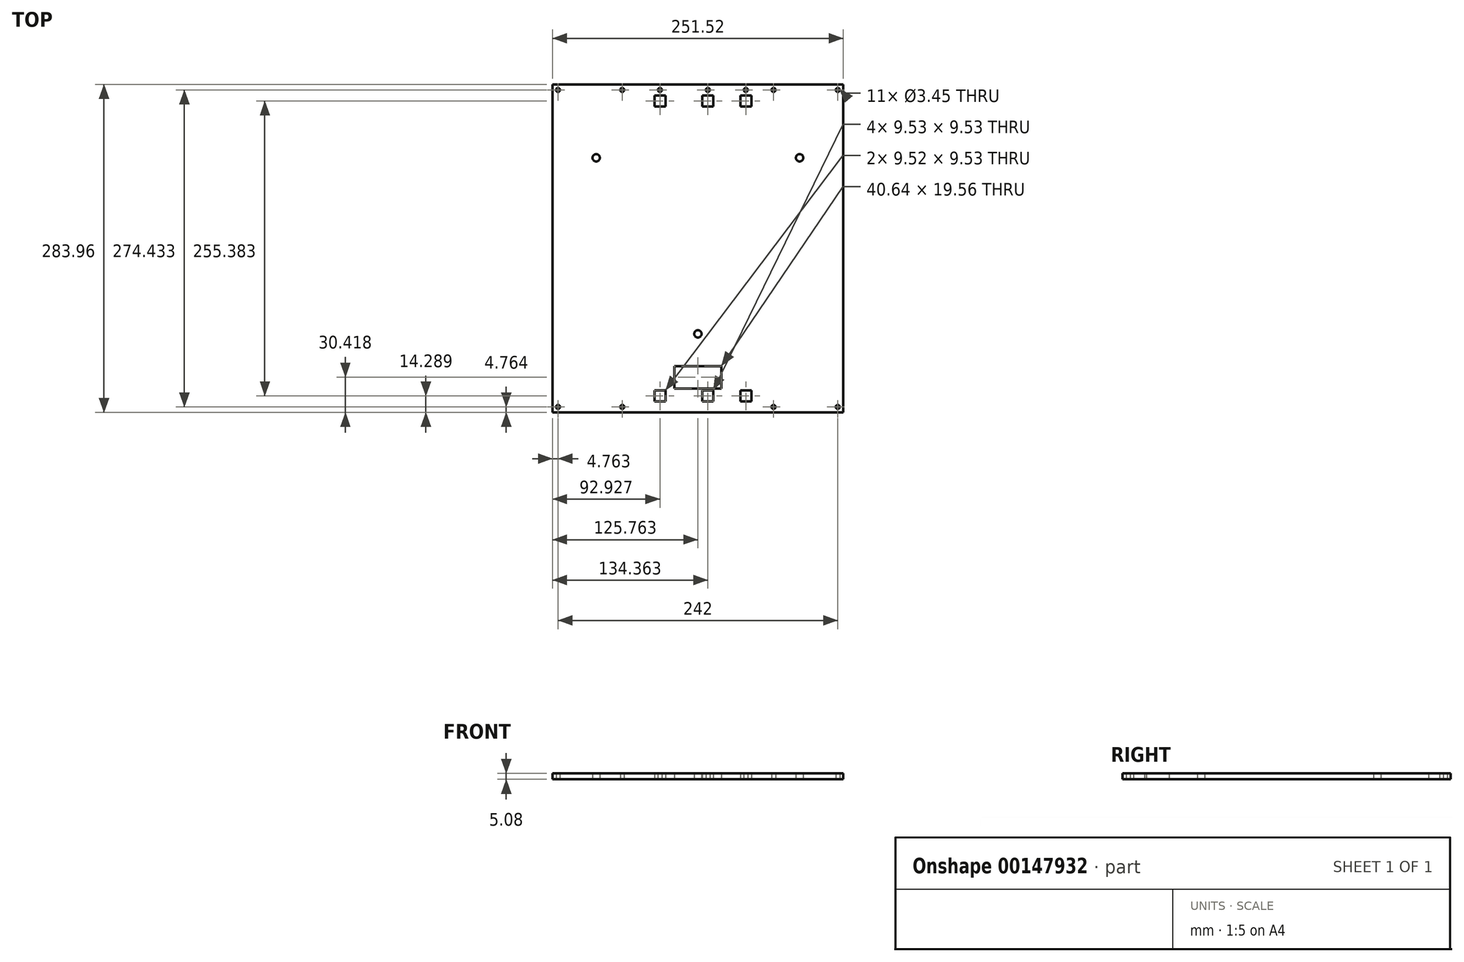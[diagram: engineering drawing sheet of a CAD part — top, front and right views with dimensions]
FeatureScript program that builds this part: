
annotation { "Feature Type Name" : "Feature", "Feature Type Description" : "" }
export const myFeature = defineFeature(function(context is Context, id is Id, definition is map)
    precondition{}
    {
        {
            var Q0;
            Q0=qCreatedBy(makeId("Top.planeOp"),FACE);
            var sketch = newSketch(context, id + "F0", { "sketchPlane" : qUnion([Q0])});
            skLineSegment(sketch, "E0.bottom", {"start": v(0, 0) * mm, "end": v(251.52, 0) * mm});
            skLineSegment(sketch, "E0.top", {"start": v(0, -283.96) * mm, "end": v(251.52, -283.96) * mm});
            skLineSegment(sketch, "E0.left", {"start": v(0, 0) * mm, "end": v(0, -283.96) * mm});
            skLineSegment(sketch, "E0.right", {"start": v(251.52, 0) * mm, "end": v(251.52, -283.96) * mm});
            skLineSegment(sketch, "E1", {"start": v(4.76, 0) * mm, "end": v(4.76, -4.76) * mm, "construction": true});
            skLineSegment(sketch, "E2", {"start": v(4.76, -4.76) * mm, "end": v(0, -4.76) * mm, "construction": true});
            skLineSegment(sketch, "E3", {"start": v(4.76, -4.76) * mm, "end": v(60.33, -4.76) * mm, "construction": true});
            skCircle(sketch, "E4", {"center": v(4.76, -4.76) * mm, "radius": 1.73 * mm});
            skCircle(sketch, "E5", {"center": v(60.33, -4.76) * mm, "radius": 1.73 * mm});
            skLineSegment(sketch, "E6", {"start": v(251.52, -4.76) * mm, "end": v(246.76, -4.76) * mm, "construction": true});
            skLineSegment(sketch, "E7", {"start": v(246.76, -4.76) * mm, "end": v(191.2, -4.76) * mm, "construction": true});
            skLineSegment(sketch, "E8", {"start": v(191.2, -4.76) * mm, "end": v(176.6, -4.76) * mm, "construction": true});
            skCircle(sketch, "E9", {"center": v(191.2, -4.76) * mm, "radius": 1.73 * mm});
            skCircle(sketch, "E10", {"center": v(246.76, -4.76) * mm, "radius": 1.73 * mm});
            skLineSegment(sketch, "E11", {"start": v(4.76, -283.96) * mm, "end": v(4.76, -279.2) * mm, "construction": true});
            skLineSegment(sketch, "E12", {"start": v(4.76, -279.2) * mm, "end": v(60.33, -279.2) * mm, "construction": true});
            skLineSegment(sketch, "E13", {"start": v(191.2, -279.2) * mm, "end": v(246.76, -279.2) * mm, "construction": true});
            skLineSegment(sketch, "E14", {"start": v(246.76, -279.2) * mm, "end": v(251.52, -279.2) * mm, "construction": true});
            skCircle(sketch, "E15", {"center": v(4.76, -279.2) * mm, "radius": 1.73 * mm});
            skCircle(sketch, "E16", {"center": v(60.33, -279.2) * mm, "radius": 1.73 * mm});
            skCircle(sketch, "E17", {"center": v(191.2, -279.2) * mm, "radius": 1.73 * mm});
            skCircle(sketch, "E18", {"center": v(246.76, -279.2) * mm, "radius": 1.73 * mm});
            skLineSegment(sketch, "E19", {"start": v(60.33, -4.76) * mm, "end": v(92.93, -4.76) * mm, "construction": true});
            skLineSegment(sketch, "E20", {"start": v(176.6, -4.76) * mm, "end": v(157.8, -4.76) * mm, "construction": true});
            skLineSegment(sketch, "E21", {"start": v(92.93, -4.76) * mm, "end": v(157.8, -4.76) * mm, "construction": true});
            skCircle(sketch, "E22", {"center": v(92.93, -4.76) * mm, "radius": 1.73 * mm});
            skCircle(sketch, "E23", {"center": v(134.36, -4.76) * mm, "radius": 1.73 * mm});
            skCircle(sketch, "E24", {"center": v(167.2, -4.76) * mm, "radius": 1.73 * mm});
            skLineSegment(sketch, "E25", {"start": v(92.93, -4.76) * mm, "end": v(92.93, -9.53) * mm, "construction": true});
            skLineSegment(sketch, "E26", {"start": v(134.36, -4.76) * mm, "end": v(134.36, -9.52) * mm, "construction": true});
            skLineSegment(sketch, "E27", {"start": v(167.2, -4.76) * mm, "end": v(167.2, -9.52) * mm, "construction": true});
            skLineSegment(sketch, "E28.bottom", {"start": v(88.17, -9.53) * mm, "end": v(97.7, -9.53) * mm});
            skLineSegment(sketch, "E28.top", {"start": v(88.17, -19.05) * mm, "end": v(97.7, -19.05) * mm});
            skLineSegment(sketch, "E28.left", {"start": v(88.17, -9.53) * mm, "end": v(88.17, -19.05) * mm});
            skLineSegment(sketch, "E28.right", {"start": v(97.7, -9.53) * mm, "end": v(97.7, -19.05) * mm});
            skLineSegment(sketch, "E29.bottom", {"start": v(129.6, -9.52) * mm, "end": v(139.12, -9.52) * mm});
            skLineSegment(sketch, "E29.top", {"start": v(129.6, -19.05) * mm, "end": v(139.12, -19.05) * mm});
            skLineSegment(sketch, "E29.left", {"start": v(129.6, -9.52) * mm, "end": v(129.6, -19.05) * mm});
            skLineSegment(sketch, "E29.right", {"start": v(139.12, -9.52) * mm, "end": v(139.12, -19.05) * mm});
            skLineSegment(sketch, "E30.bottom", {"start": v(162.43, -9.52) * mm, "end": v(171.96, -9.52) * mm});
            skLineSegment(sketch, "E30.top", {"start": v(162.43, -19.05) * mm, "end": v(171.96, -19.05) * mm});
            skLineSegment(sketch, "E30.left", {"start": v(162.43, -9.52) * mm, "end": v(162.43, -19.05) * mm});
            skLineSegment(sketch, "E30.right", {"start": v(171.96, -9.52) * mm, "end": v(171.96, -19.05) * mm});
            skLineSegment(sketch, "E31", {"start": v(125.76, 0) * mm, "end": v(125.76, -114.3) * mm, "construction": true});
            skCircle(sketch, "E32", {"center": v(125.76, -114.3) * mm, "radius": 114.3 * mm, "construction": true});
            skCircle(sketch, "E33.cCircle", {"center": v(125.76, -114.3) * mm, "radius": 50.8 * mm, "construction": true});
            skLineSegment(sketch, "E33.0", {"start": v(37.77, -63.5) * mm, "end": v(213.75, -63.5) * mm, "construction": true});
            skLineSegment(sketch, "E33.1", {"start": v(213.75, -63.5) * mm, "end": v(125.76, -215.9) * mm, "construction": true});
            skLineSegment(sketch, "E33.2", {"start": v(125.76, -215.9) * mm, "end": v(37.77, -63.5) * mm, "construction": true});
            skPoint(sketch, "E33.0.midPoint", {"position": v(125.76, -63.5) * mm});
            skCircle(sketch, "E34", {"center": v(213.75, -63.5) * mm, "radius": 12.7 * mm, "construction": true});
            skCircle(sketch, "E35", {"center": v(125.76, -215.9) * mm, "radius": 3.18 * mm});
            skCircle(sketch, "E36", {"center": v(37.77, -63.5) * mm, "radius": 3.18 * mm});
            skCircle(sketch, "E37", {"center": v(213.75, -63.5) * mm, "radius": 3.18 * mm});
            skLineSegment(sketch, "E38", {"start": v(125.76, -114.3) * mm, "end": v(125.76, -228.6) * mm, "construction": true});
            skLineSegment(sketch, "E39", {"start": v(125.76, -228.6) * mm, "end": v(125.76, -253.54) * mm, "construction": true});
            skLineSegment(sketch, "E40.bottom", {"start": v(146.08, -243.76) * mm, "end": v(105.44, -243.76) * mm});
            skLineSegment(sketch, "E40.top", {"start": v(146.08, -263.32) * mm, "end": v(105.44, -263.32) * mm});
            skLineSegment(sketch, "E40.left", {"start": v(146.08, -243.76) * mm, "end": v(146.08, -263.32) * mm});
            skLineSegment(sketch, "E40.right", {"start": v(105.44, -243.76) * mm, "end": v(105.44, -263.32) * mm});
            skPoint(sketch, "E40.middle", {"position": v(125.76, -253.54) * mm});
            skLineSegment(sketch, "E41", {"start": v(146.08, -253.54) * mm, "end": v(136.66, -253.54) * mm, "construction": true});
            skLineSegment(sketch, "E42", {"start": v(136.66, -253.54) * mm, "end": v(125.76, -114.3) * mm, "construction": true});
            skLineSegment(sketch, "E43", {"start": v(125.76, -263.32) * mm, "end": v(125.76, -283.96) * mm, "construction": true});
            skLineSegment(sketch, "E44", {"start": v(60.33, -279.2) * mm, "end": v(92.93, -279.2) * mm, "construction": true});
            skLineSegment(sketch, "E45", {"start": v(92.93, -279.2) * mm, "end": v(92.93, -274.43) * mm, "construction": true});
            skLineSegment(sketch, "E46", {"start": v(191.2, -279.2) * mm, "end": v(167.2, -279.2) * mm, "construction": true});
            skLineSegment(sketch, "E47", {"start": v(167.2, -279.2) * mm, "end": v(167.2, -274.43) * mm, "construction": true});
            skLineSegment(sketch, "E48.bottom", {"start": v(88.17, -274.43) * mm, "end": v(97.7, -274.43) * mm});
            skLineSegment(sketch, "E48.top", {"start": v(88.17, -264.9) * mm, "end": v(97.7, -264.9) * mm});
            skLineSegment(sketch, "E48.left", {"start": v(88.17, -274.43) * mm, "end": v(88.17, -264.9) * mm});
            skLineSegment(sketch, "E48.right", {"start": v(97.7, -274.43) * mm, "end": v(97.7, -264.9) * mm});
            skLineSegment(sketch, "E49.bottom", {"start": v(162.43, -274.43) * mm, "end": v(171.96, -274.43) * mm});
            skLineSegment(sketch, "E49.top", {"start": v(162.43, -264.9) * mm, "end": v(171.96, -264.9) * mm});
            skLineSegment(sketch, "E49.left", {"start": v(162.43, -274.43) * mm, "end": v(162.43, -264.9) * mm});
            skLineSegment(sketch, "E49.right", {"start": v(171.96, -274.43) * mm, "end": v(171.96, -264.9) * mm});
            skLineSegment(sketch, "E50", {"start": v(92.93, -279.2) * mm, "end": v(134.36, -279.2) * mm, "construction": true});
            skLineSegment(sketch, "E51", {"start": v(134.36, -279.2) * mm, "end": v(167.2, -279.2) * mm, "construction": true});
            skLineSegment(sketch, "E52", {"start": v(134.36, -279.2) * mm, "end": v(134.36, -274.43) * mm, "construction": true});
            skLineSegment(sketch, "E53.bottom", {"start": v(129.6, -274.43) * mm, "end": v(139.12, -274.43) * mm});
            skLineSegment(sketch, "E53.top", {"start": v(129.6, -264.9) * mm, "end": v(139.12, -264.9) * mm});
            skLineSegment(sketch, "E53.left", {"start": v(129.6, -274.43) * mm, "end": v(129.6, -264.9) * mm});
            skLineSegment(sketch, "E53.right", {"start": v(139.12, -274.43) * mm, "end": v(139.12, -264.9) * mm});
            skSolve(sketch);
        }
        {
            var Q0;
            Q0=qSketchRegion(id+"F0",true);
            extrude(context, id + "F1", {"entities" : qUnion([Q0]), "depth" : 5.08 * mm});
        }
    });
